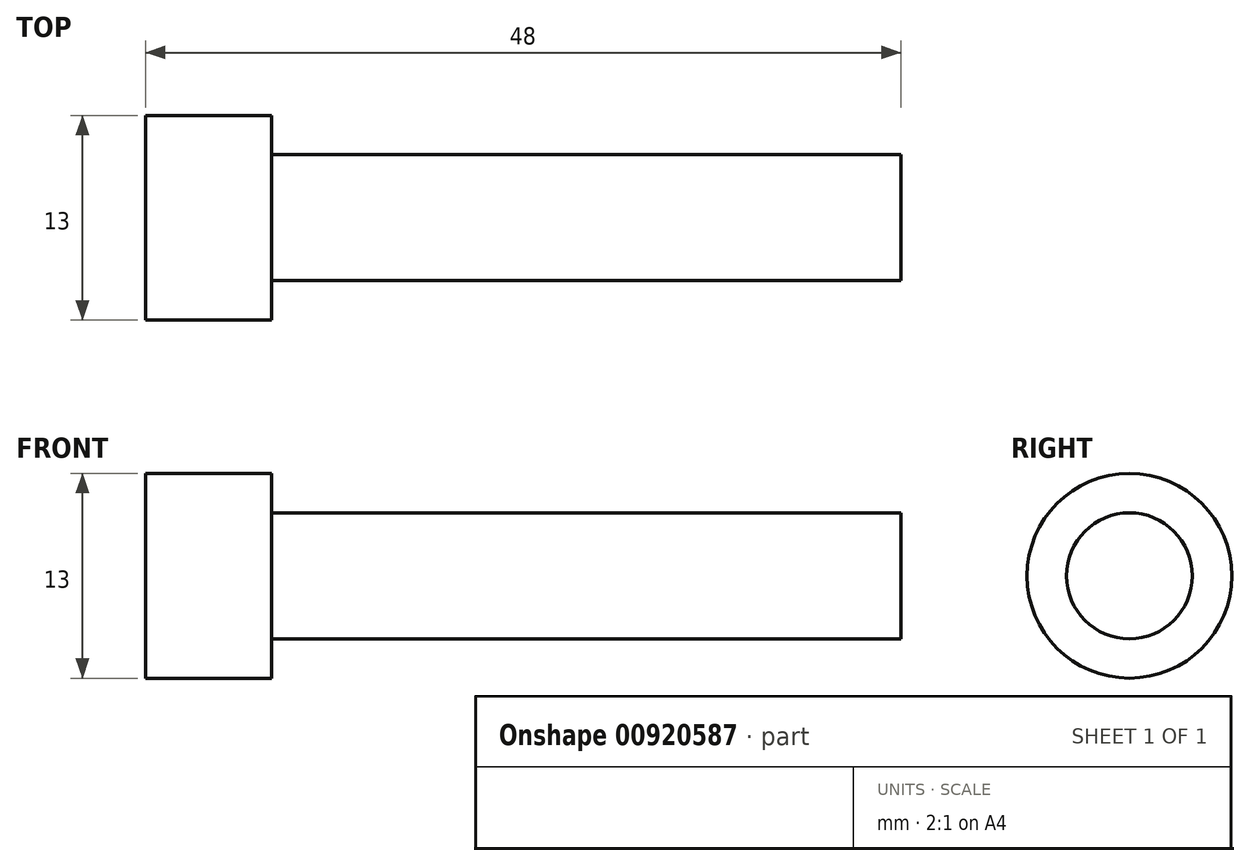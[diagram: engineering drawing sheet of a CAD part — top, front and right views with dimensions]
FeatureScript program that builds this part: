
annotation { "Feature Type Name" : "Feature", "Feature Type Description" : "" }
export const myFeature = defineFeature(function(context is Context, id is Id, definition is map)
    precondition{}
    {
        {
            var Q0;
            Q0=qCreatedBy(makeId("Front.planeOp"),FACE);
            var sketch = newSketch(context, id + "F0", { "sketchPlane" : qUnion([Q0])});
            skLineSegment(sketch, "E0", {"start": v(-21.8, 0) * mm, "end": v(0, 0) * mm, "construction": true});
            skLineSegment(sketch, "E1", {"start": v(0, 0) * mm, "end": v(0, 6.5) * mm});
            skLineSegment(sketch, "E2", {"start": v(0, 6.5) * mm, "end": v(8, 6.5) * mm});
            skLineSegment(sketch, "E3", {"start": v(8, 6.5) * mm, "end": v(8, 4) * mm});
            skLineSegment(sketch, "E4", {"start": v(8, 4) * mm, "end": v(48, 4) * mm});
            skLineSegment(sketch, "E5", {"start": v(48, 4) * mm, "end": v(48, 0) * mm});
            skLineSegment(sketch, "E6", {"start": v(0, 0) * mm, "end": v(48, 0) * mm});
            skSolve(sketch);
        }
        {
            var Q0;
            Q0=makeQuery(id+"F0.imprint","IMPRINT",FACE,{"disambiguationData":[TD([[makeQuery(id+"F0.imprint","IMPRINT",EDGE,{"derivedFrom":sQuery(id+"F0.wireOp",EDGE,"E1")}),-1.0]])]});
            var Q1;
            Q1=sQuery(id+"F0.wireOp",EDGE,"E0");
            revolve(context, id + "F1", {"surfaceOperationType" : NewSurfaceOperationType.NEW, "entities" : qUnion([Q0]), "axis" : qUnion([Q1]), "revolveType" : RevolveType.FULL});
        }
    });
